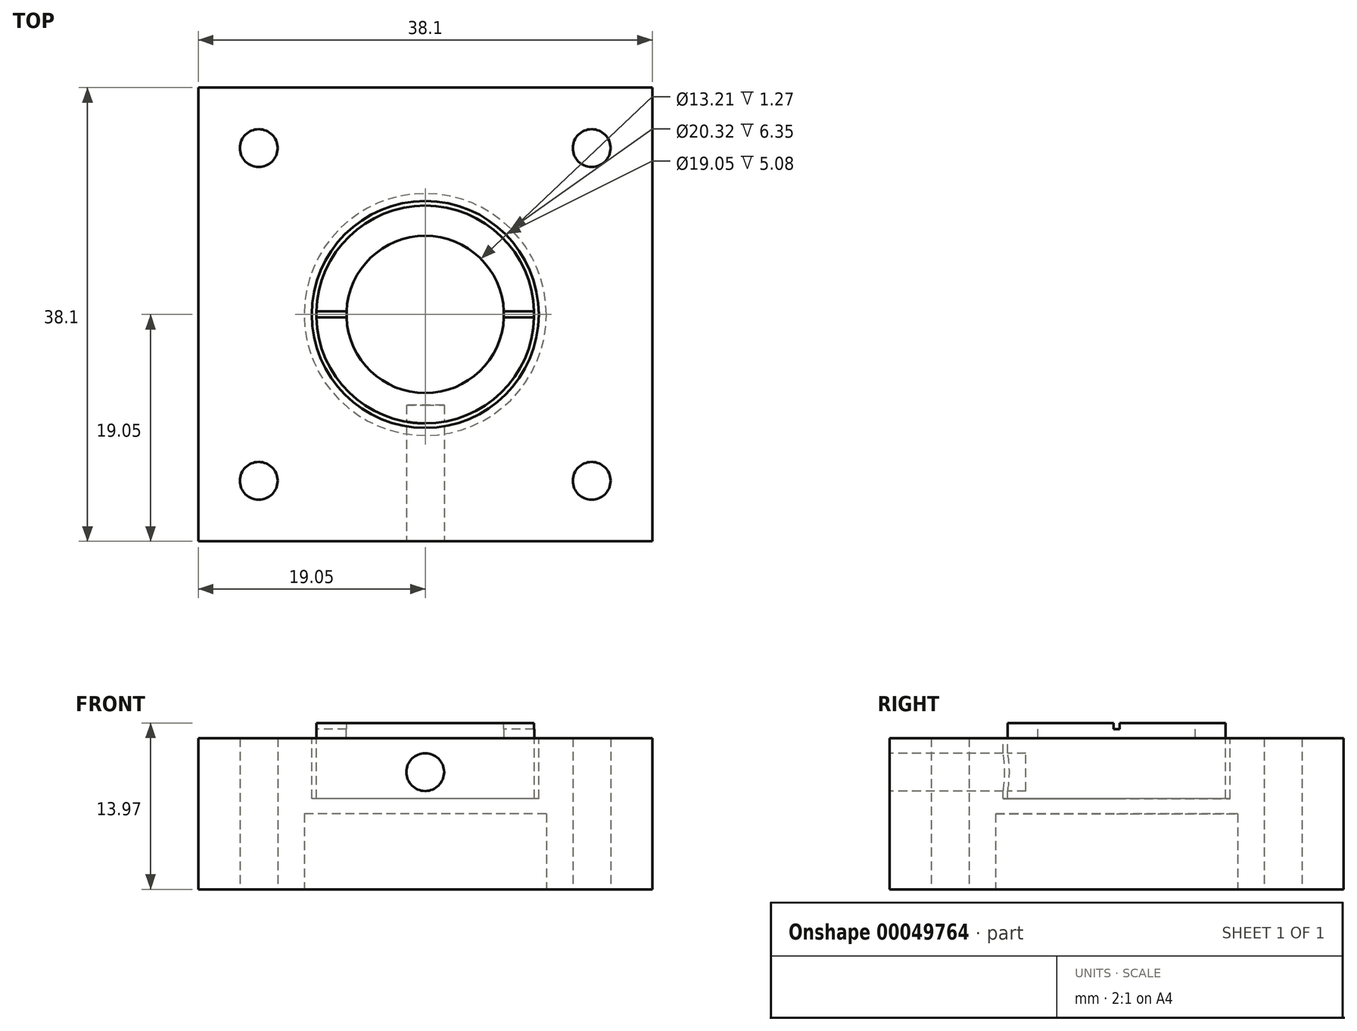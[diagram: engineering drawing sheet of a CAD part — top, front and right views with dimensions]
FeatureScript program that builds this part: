
annotation { "Feature Type Name" : "Feature", "Feature Type Description" : "" }
export const myFeature = defineFeature(function(context is Context, id is Id, definition is map)
    precondition{}
    {
        {
            var Q0;
            Q0=qCreatedBy(makeId("Top.planeOp"),FACE);
            var sketch = newSketch(context, id + "F0", { "sketchPlane" : qUnion([Q0])});
            skLineSegment(sketch, "E0.rect.bottom", {"start": v(19.05, -19.05) * mm, "end": v(-19.05, -19.05) * mm});
            skLineSegment(sketch, "E0.rect.top", {"start": v(19.05, 19.05) * mm, "end": v(-19.05, 19.05) * mm});
            skLineSegment(sketch, "E0.rect.left", {"start": v(19.05, -19.05) * mm, "end": v(19.05, 19.05) * mm});
            skLineSegment(sketch, "E0.rect.right", {"start": v(-19.05, -19.05) * mm, "end": v(-19.05, 19.05) * mm});
            skPoint(sketch, "E0.rect.middle", {"position": v(0, 0) * mm});
            skSolve(sketch);
        }
        {
            var Q0;
            Q0=makeQuery(id+"F0.imprint","IMPRINT",FACE,{"disambiguationData":[TD([[makeQuery(id+"F0.imprint","IMPRINT",EDGE,{"derivedFrom":sQuery(id+"F0.wireOp",EDGE,"E0.rect.bottom")}),-1.0]])]});
            extrude(context, id + "F1", {"entities" : qUnion([Q0]), "depth" : 12.7 * mm});
        }
        {
            var Q0;
            Q0=makeQuery(id+"F1.opExtrude","CAP_FACE",FACE,{"disambiguationData":[OSD([sQuery(id+"F0.wireOp",EDGE,"E0.rect.bottom"),sQuery(id+"F0.wireOp",EDGE,"E0.rect.top"),sQuery(id+"F0.wireOp",EDGE,"E0.rect.left"),sQuery(id+"F0.wireOp",EDGE,"E0.rect.right")])],"isStart":false});
            var sketch = newSketch(context, id + "F2", { "sketchPlane" : qUnion([Q0])});
            skCircle(sketch, "E1", {"center": v(0, 0) * mm, "radius": 9.53 * mm});
            skSolve(sketch);
        }
        {
            var Q0;
            Q0=makeQuery(id+"F0.imprint","IMPRINT",FACE,{"disambiguationData":[TD([[makeQuery(id+"F0.imprint","IMPRINT",EDGE,{"derivedFrom":sQuery(id+"F0.wireOp",EDGE,"E0.rect.bottom")}),-1.0]])]});
            var sketch = newSketch(context, id + "F3", { "sketchPlane" : qUnion([Q0])});
            skCircle(sketch, "E2", {"center": v(0, 0) * mm, "radius": 10.16 * mm});
            skSolve(sketch);
        }
        {
            var Q0;
            Q0 = qSketchRegion(id + "F3", true);
            extrude(context, id + "F4", {"entities" : qUnion([Q0]), "operationType" : NewBodyOperationType.REMOVE, "depth" : 6.35 * mm});
        }
        {
            var Q0;
            Q0 = qSketchRegion(id + "F2", true);
            extrude(context, id + "F5", {"entities" : qUnion([Q0]), "operationType" : NewBodyOperationType.REMOVE, "oppositeDirection" : true, "depth" : 5.08 * mm});
        }
        {
            var Q0;
            Q0=qCreatedBy(makeId("Top.planeOp"),FACE);
            var sketch = newSketch(context, id + "F6", { "sketchPlane" : qUnion([Q0])});
            skCircle(sketch, "E3", {"center": v(-13.97, -13.97) * mm, "radius": 1.59 * mm});
            skCircle(sketch, "E4.MirrorC", {"center": v(13.97, -13.97) * mm, "radius": 1.59 * mm});
            skCircle(sketch, "E5.MirrorC", {"center": v(13.97, 13.97) * mm, "radius": 1.59 * mm});
            skCircle(sketch, "E6.MirrorC", {"center": v(-13.97, 13.97) * mm, "radius": 1.59 * mm});
            skSolve(sketch);
        }
        {
            var Q0;
            Q0 = qSketchRegion(id + "F6", true);
            extrude(context, id + "F7", {"entities" : qUnion([Q0]), "operationType" : NewBodyOperationType.REMOVE, "depth" : 25.4 * mm});
        }
        {
            var Q0;
            Q0=makeQuery(id+"F2.imprint","IMPRINT",FACE,{"disambiguationData":[TD([[makeQuery(id+"F2.imprint","IMPRINT",EDGE,{"derivedFrom":sQuery(id+"F2.wireOp",EDGE,"E1")}),-1.0]])]});
            var sketch = newSketch(context, id + "F8", { "sketchPlane" : qUnion([Q0])});
            skCircle(sketch, "E7", {"center": v(0, 0) * mm, "radius": 9.14 * mm});
            skSolve(sketch);
        }
        {
            var Q0;
            Q0 = qSketchRegion(id + "F8", true);
            extrude(context, id + "F9", {"entities" : qUnion([Q0]), "oppositeDirection" : true, "depth" : 5.08 * mm, "hasSecondDirection" : true, "secondDirectionOppositeDirection" : false, "secondDirectionDepth" : 1.27 * mm});
        }
        {
            var Q0;
            Q0=makeQuery(id+"F9.opExtrude","CAP_FACE",FACE,{"disambiguationData":[OSD([sQuery(id+"F8.wireOp",EDGE,"E7")])],"isStart":true});
            var sketch = newSketch(context, id + "F10", { "sketchPlane" : qUnion([Q0])});
            skCircle(sketch, "E8", {"center": v(0, 0) * mm, "radius": 6.6 * mm});
            skSolve(sketch);
        }
        {
            var Q0;
            Q0=makeQuery(id+"F10.imprint","IMPRINT",FACE,{"disambiguationData":[TD([[makeQuery(id+"F10.imprint","IMPRINT",EDGE,{"derivedFrom":sQuery(id+"F10.wireOp",EDGE,"E8")}),1.0]])]});
            extrude(context, id + "F11", {"entities" : qUnion([Q0]), "operationType" : NewBodyOperationType.REMOVE, "oppositeDirection" : true, "depth" : 1.27 * mm});
        }
        {
            var Q0;
            Q0=makeQuery(id+"F1.opExtrude","SWEPT_FACE",FACE,{"disambiguationData":[OSD([sQuery(id+"F0.wireOp",EDGE,"E0.rect.bottom")])]});
            var sketch = newSketch(context, id + "F12", { "sketchPlane" : qUnion([Q0])});
            skCircle(sketch, "E9", {"center": v(0, 9.84) * mm, "radius": 1.59 * mm});
            skSolve(sketch);
        }
        {
            var Q0;
            Q0 = qSketchRegion(id + "F12", true);
            extrude(context, id + "F13", {"entities" : qUnion([Q0]), "operationType" : NewBodyOperationType.REMOVE, "oppositeDirection" : true, "depth" : 11.43 * mm});
        }
        {
            var Q0;
            Q0=makeQuery(id+"F9.opExtrude","CAP_FACE",FACE,{"disambiguationData":[OSD([sQuery(id+"F8.wireOp",EDGE,"E7")])],"isStart":true});
            var sketch = newSketch(context, id + "F14", { "sketchPlane" : qUnion([Q0])});
            skLineSegment(sketch, "E10.bottom", {"start": v(9.53, -0.25) * mm, "end": v(-9.53, -0.25) * mm});
            skLineSegment(sketch, "E10.top", {"start": v(9.53, 0.25) * mm, "end": v(-9.53, 0.25) * mm});
            skLineSegment(sketch, "E10.left", {"start": v(9.53, -0.25) * mm, "end": v(9.53, 0.25) * mm});
            skLineSegment(sketch, "E10.right", {"start": v(-9.53, -0.25) * mm, "end": v(-9.53, 0.25) * mm});
            skPoint(sketch, "E10.middle", {"position": v(0, 0) * mm});
            skSolve(sketch);
        }
        {
            var Q0;
            Q0 = qSketchRegion(id + "F14", true);
            extrude(context, id + "F15", {"entities" : qUnion([Q0]), "operationType" : NewBodyOperationType.REMOVE, "oppositeDirection" : true, "depth" : 0.5 * mm});
        }
    });
